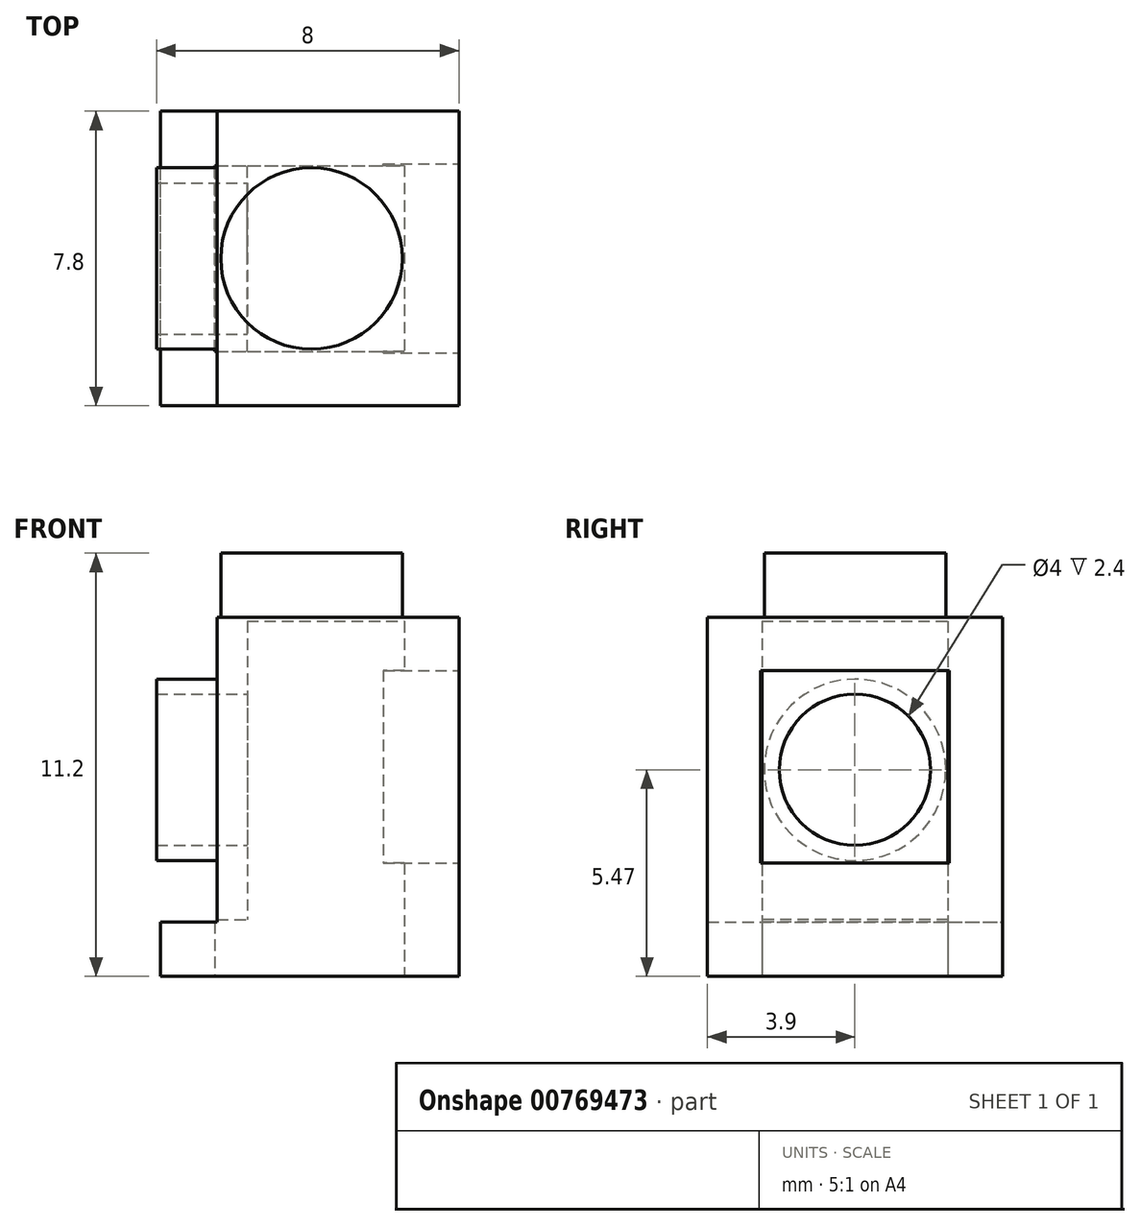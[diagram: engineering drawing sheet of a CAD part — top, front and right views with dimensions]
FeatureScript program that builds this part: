
annotation { "Feature Type Name" : "Feature", "Feature Type Description" : "" }
export const myFeature = defineFeature(function(context is Context, id is Id, definition is map)
    precondition{}
    {
        {
            var Q0;
            Q0=qCreatedBy(makeId("Front.planeOp"),FACE);
            var sketch = newSketch(context, id + "F0", { "sketchPlane" : qUnion([Q0])});
            skLineSegment(sketch, "E0", {"start": v(0, 0) * mm, "end": v(7.9, 0) * mm});
            skLineSegment(sketch, "E1", {"start": v(7.9, 0) * mm, "end": v(7.9, 9.5) * mm});
            skLineSegment(sketch, "E2", {"start": v(7.9, 9.5) * mm, "end": v(1.5, 9.5) * mm});
            skLineSegment(sketch, "E3", {"start": v(0, 0) * mm, "end": v(0, 1.44) * mm});
            skLineSegment(sketch, "E4", {"start": v(0, 1.44) * mm, "end": v(1.5, 1.44) * mm});
            skLineSegment(sketch, "E5", {"start": v(1.5, 1.44) * mm, "end": v(1.5, 9.5) * mm});
            skSolve(sketch);
        }
        {
            var Q0;
            Q0 = qSketchRegion(id + "F0", true);
            extrude(context, id + "F1", {"entities" : qUnion([Q0]), "depth" : 7.8 * mm, "offsetDistance" : 25 * mm});
        }
        {
            var Q0;
            Q0=makeQuery(id+"F1.opExtrude","SWEPT_FACE",FACE,{"disambiguationData":[OSD([sQuery(id+"F0.wireOp",EDGE,"E2")])]});
            var sketch = newSketch(context, id + "F2", { "sketchPlane" : qUnion([Q0])});
            skCircle(sketch, "E6", {"center": v(4, -3.9) * mm, "radius": 2.4 * mm});
            skSolve(sketch);
        }
        {
            var Q0;
            Q0 = qSketchRegion(id + "F2", true);
            extrude(context, id + "F3", {"entities" : qUnion([Q0]), "operationType" : NewBodyOperationType.ADD, "depth" : 1.7 * mm, "offsetDistance" : 25 * mm});
        }
        {
            var Q0;
            Q0=makeQuery(id+"F1.opExtrude","SWEPT_FACE",FACE,{"disambiguationData":[OSD([sQuery(id+"F0.wireOp",EDGE,"E0")])]});
            var sketch = newSketch(context, id + "F4", { "sketchPlane" : qUnion([Q0])});
            skLineSegment(sketch, "E7.0", {"start": v(1.44, 6.36) * mm, "end": v(6.46, 6.36) * mm});
            skLineSegment(sketch, "E7.1", {"start": v(1.44, 6.36) * mm, "end": v(1.44, 1.44) * mm});
            skLineSegment(sketch, "E7.2", {"start": v(1.44, 1.44) * mm, "end": v(6.46, 1.44) * mm});
            skLineSegment(sketch, "E7.3", {"start": v(6.46, 6.36) * mm, "end": v(6.46, 1.44) * mm});
            skSolve(sketch);
        }
        {
            var Q0;
            Q0 = qSketchRegion(id + "F4", true);
            extrude(context, id + "F5", {"entities" : qUnion([Q0]), "operationType" : NewBodyOperationType.REMOVE, "oppositeDirection" : true, "depth" : 1.5 * mm, "offsetDistance" : 25 * mm});
        }
        {
            var Q0;
            Q0=makeQuery(id+"F5.boolean.opBoolean","COPY",FACE,{"derivedFrom":makeQuery(id+"F5.opExtrude","CAP_FACE",FACE,{"disambiguationData":[OSD([sQuery(id+"F4.wireOp",EDGE,"E7.0"),sQuery(id+"F4.wireOp",EDGE,"E7.1"),sQuery(id+"F4.wireOp",EDGE,"E7.2"),sQuery(id+"F4.wireOp",EDGE,"E7.3")])],"isStart":false})});
            var sketch = newSketch(context, id + "F6", { "sketchPlane" : qUnion([Q0])});
            skLineSegment(sketch, "E8", {"start": v(2.3, 6.36) * mm, "end": v(2.3, 1.44) * mm});
            skLineSegment(sketch, "E9", {"start": v(2.3, 1.44) * mm, "end": v(6.46, 1.44) * mm});
            skLineSegment(sketch, "E10", {"start": v(6.46, 1.44) * mm, "end": v(6.46, 6.36) * mm});
            skLineSegment(sketch, "E11", {"start": v(6.46, 6.36) * mm, "end": v(2.3, 6.36) * mm});
            skSolve(sketch);
        }
        {
            var Q0;
            Q0 = qSketchRegion(id + "F6", true);
            extrude(context, id + "F7", {"entities" : qUnion([Q0]), "operationType" : NewBodyOperationType.REMOVE, "oppositeDirection" : true, "depth" : 7.9 * mm, "offsetDistance" : 25 * mm});
        }
        {
            var Q0;
            Q0=makeQuery(id+"F1.opExtrude","SWEPT_FACE",FACE,{"disambiguationData":[OSD([sQuery(id+"F0.wireOp",EDGE,"E5")])]});
            var sketch = newSketch(context, id + "F8", { "sketchPlane" : qUnion([Q0])});
            skCircle(sketch, "E12", {"center": v(3.9, 5.47) * mm, "radius": 2.4 * mm});
            skPoint(sketch, "E12.centerSnap0", {"position": v(0, 5.47) * mm});
            skPoint(sketch, "E12.centerSnap1", {"position": v(3.9, 9.5) * mm});
            skCircle(sketch, "E13", {"center": v(3.9, 5.47) * mm, "radius": 2 * mm});
            skSolve(sketch);
        }
        {
            var Q0;
            Q0 = qSketchRegion(id + "F8", true);
            extrude(context, id + "F9", {"entities" : qUnion([Q0]), "operationType" : NewBodyOperationType.ADD, "depth" : 1.6 * mm, "offsetDistance" : 25 * mm});
        }
        {
            var Q0;
            Q0=makeQuery(id+"F8.imprint","IMPRINT",FACE,{"disambiguationData":[TD([[makeQuery(id+"F8.imprint","IMPRINT",EDGE,{"derivedFrom":sQuery(id+"F8.wireOp",EDGE,"E13")}),1.0]])]});
            extrude(context, id + "F10", {"entities" : qUnion([Q0]), "operationType" : NewBodyOperationType.REMOVE, "oppositeDirection" : true, "depth" : 1 * mm, "offsetDistance" : 25 * mm});
        }
        {
            var Q0;
            Q0=makeQuery(id+"F1.opExtrude","SWEPT_FACE",FACE,{"disambiguationData":[OSD([sQuery(id+"F0.wireOp",EDGE,"E1")])]});
            var sketch = newSketch(context, id + "F11", { "sketchPlane" : qUnion([Q0])});
            skLineSegment(sketch, "E14.0", {"start": v(-1.4, 3) * mm, "end": v(-1.4, 8.1) * mm});
            skLineSegment(sketch, "E14.1", {"start": v(-6.4, 8.1) * mm, "end": v(-1.4, 8.1) * mm});
            skLineSegment(sketch, "E14.2", {"start": v(-6.4, 3) * mm, "end": v(-6.4, 8.1) * mm});
            skLineSegment(sketch, "E15.0", {"start": v(-6.4, 3) * mm, "end": v(-1.4, 3) * mm});
            skSolve(sketch);
        }
        {
            var Q0;
            Q0 = qSketchRegion(id + "F11", true);
            extrude(context, id + "F12", {"entities" : qUnion([Q0]), "operationType" : NewBodyOperationType.REMOVE, "oppositeDirection" : true, "depth" : 2 * mm, "offsetDistance" : 25 * mm});
        }
    });
